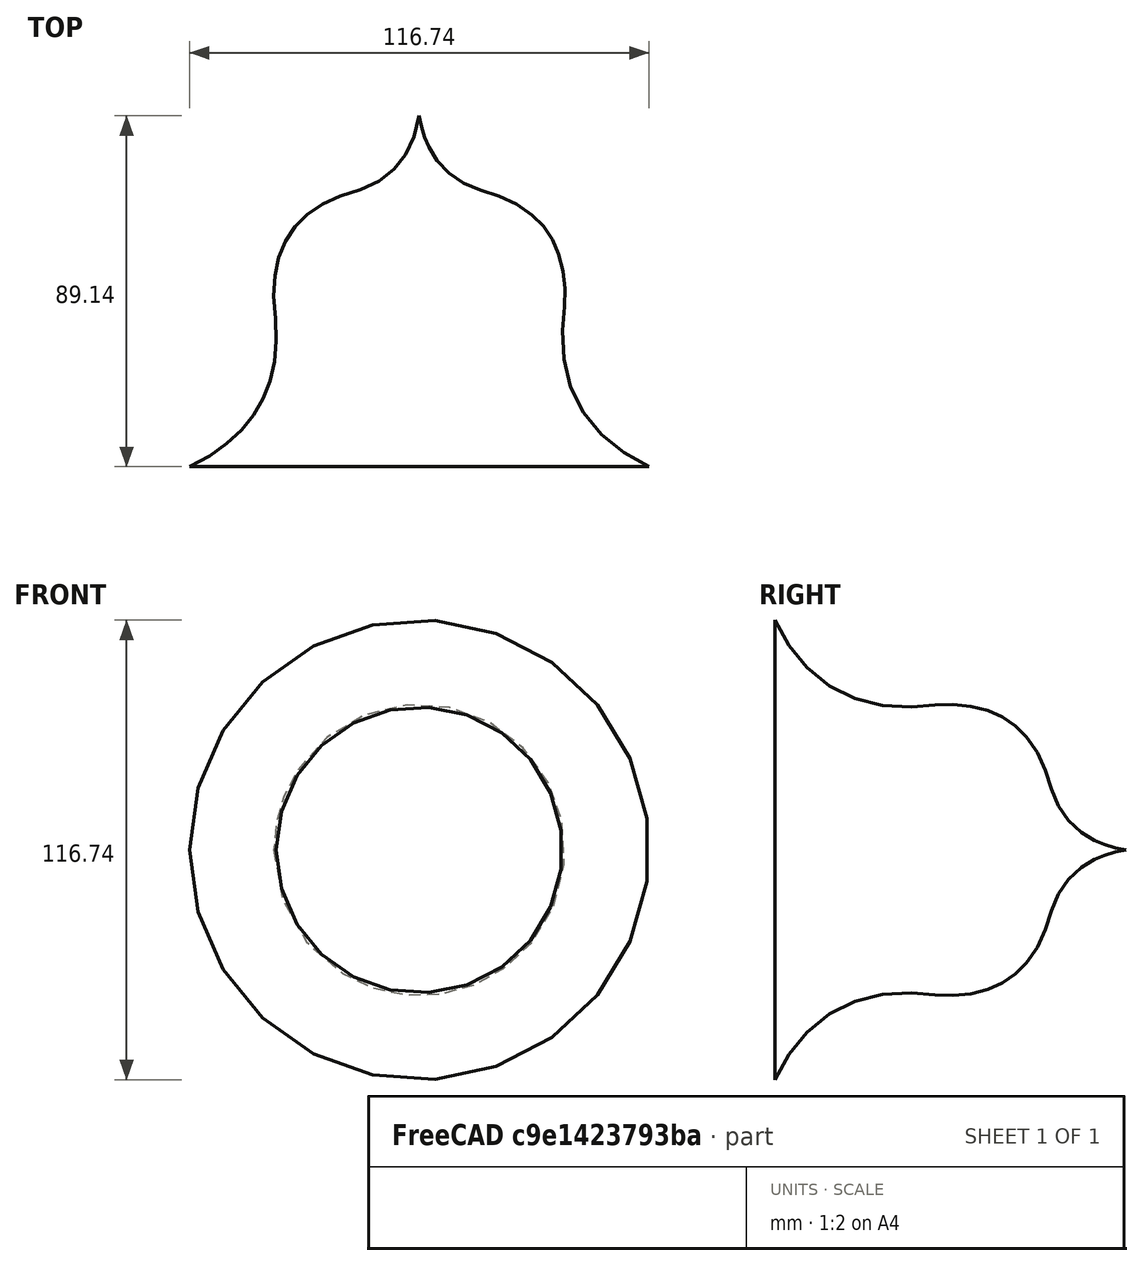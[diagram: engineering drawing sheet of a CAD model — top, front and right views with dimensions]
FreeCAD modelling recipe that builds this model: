
FCSTD DOCUMENT  (FreeCAD 0.21RUnknown)
Label: part8
License: All rights reserved
LicenseURL: http://en.wikipedia.org/wiki/All_rights_reserved
objects: Part::FeaturePython×4, Sketcher::SketchObject×2, Part::Revolution×1, App::DocumentObjectGroup×1, Part::Loft×1
note: 8 computed .brp shape members not serialized (recipe doc carries the construction recipe); baked Part::Feature solids carry a one-line shape summary decoded from their .brp

FEATURE [Sketcher::SketchObject] Sketch
  FullyConstrained = false
  sketch-geometry (4):
    g0: GeomPoint X=-7.60089 Y=35.4144 Z=0
    g1: GeomPoint X=-32.7105 Y=20.4185 Z=0
    g2: GeomPoint X=-36.801 Y=-12.3053 Z=0
    g3: GeomPoint X=-58.369 Y=-39.0793 Z=0
FEATURE [Part::Revolution] Revolve
  Angle = 360
  Axis = (0,1,0)
  Base = (0,0,0)
  FaceMakerClass = Part::FaceMakerBullseye
  Solid = false
  Source = -> Sketch
  Symmetric = false
FEATURE [Sketcher::SketchObject] Sketch001
  FullyConstrained = false
  Placement = pos=(0,0,0) rot=(0.57735,0.57735,0.57735;2.0944rad)
  sketch-geometry (1):
    g0: GeomPoint X=50.064 Y=0 Z=0
  constraints (1):
    c: PointOnObject(g0,g-1)
FEATURE [Part::FeaturePython] Revolve_child0  label="Revolve.0"  # WARN: FeaturePython — macro-defined, semantics opaque (R4)
  Base = -> Revolve
  FilterType = 1
  Invert = false
  OverrideMaxVal = 0
  WindowFrom = 80
  WindowTo = 100
  items = 0
FEATURE [Part::FeaturePython] Revolve_child1  label="Revolve.1"  # WARN: FeaturePython — macro-defined, semantics opaque (R4)
  Base = -> Revolve
  FilterType = 1
  Invert = false
  OverrideMaxVal = 0
  WindowFrom = 80
  WindowTo = 100
  items = 1
FEATURE [Part::FeaturePython] Revolve_child2  label="Revolve.2"  # WARN: FeaturePython — macro-defined, semantics opaque (R4)
  Base = -> Revolve
  FilterType = 1
  Invert = false
  OverrideMaxVal = 0
  WindowFrom = 80
  WindowTo = 100
  items = 2
FEATURE [Part::FeaturePython] Revolve_child3  label="Revolve.3"  # WARN: FeaturePython — macro-defined, semantics opaque (R4)
  Base = -> Revolve
  FilterType = 1
  Invert = false
  OverrideMaxVal = 0
  WindowFrom = 80
  WindowTo = 100
  items = 3
FEATURE [App::DocumentObjectGroup] GrExplode_Revolve  label="Exploded Revolve"
  Group = -> [Revolve_child0,Revolve_child1,Revolve_child2,Revolve_child3]
FEATURE [Part::Loft] Loft
  Closed = false
  MaxDegree = 2
  Ruled = false
  Sections = -> [Sketch001,Revolve_child0,Revolve_child1,Revolve_child2,Revolve_child3]
  Solid = false
